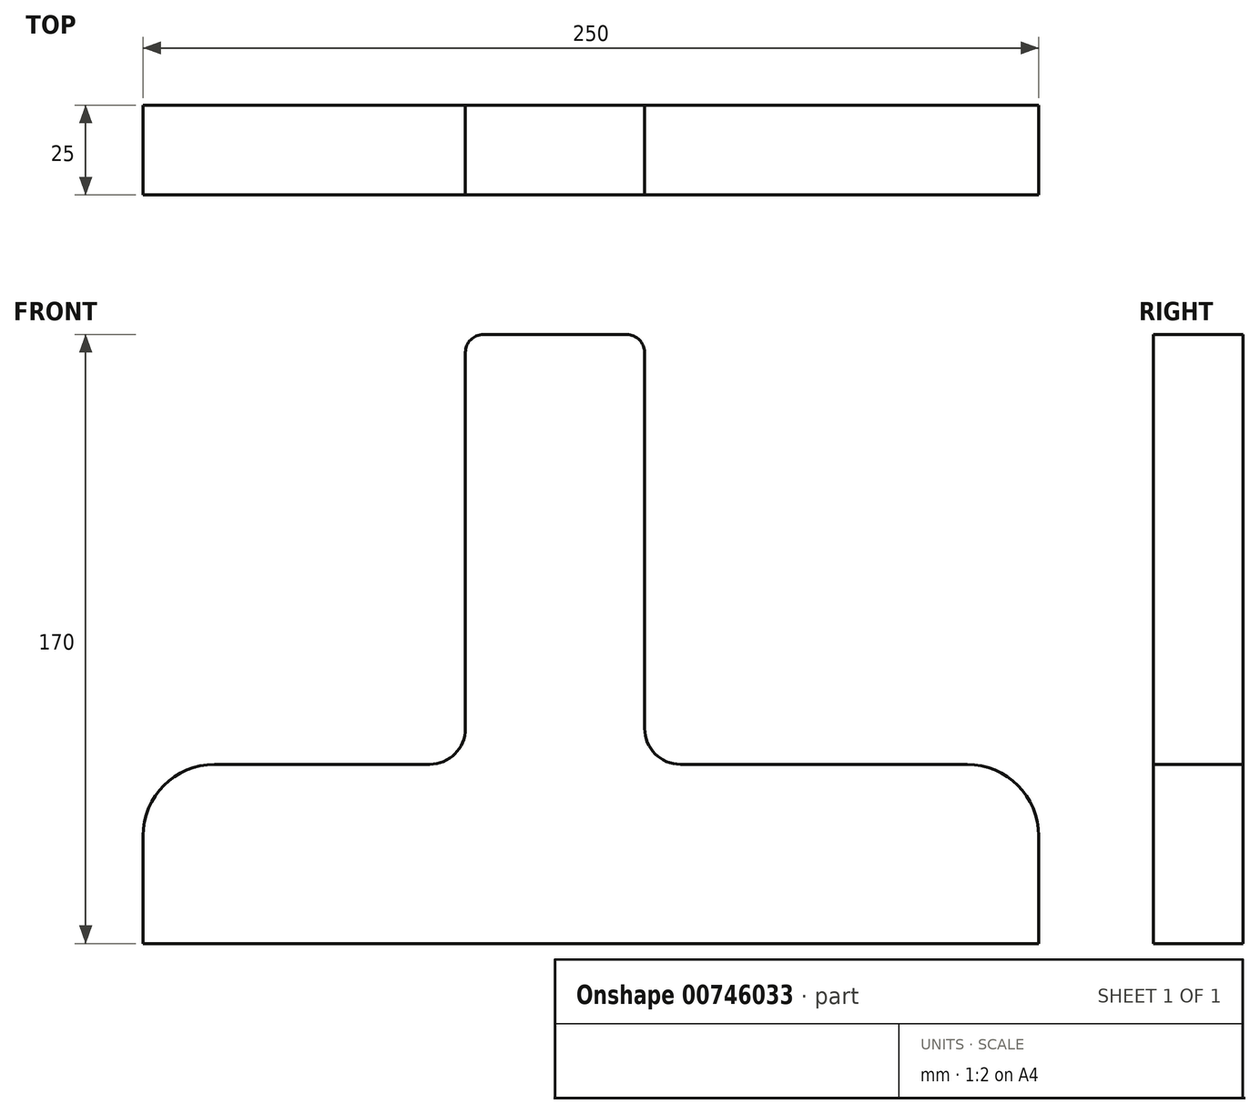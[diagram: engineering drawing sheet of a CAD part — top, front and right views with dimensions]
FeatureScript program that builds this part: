
annotation { "Feature Type Name" : "Feature", "Feature Type Description" : "" }
export const myFeature = defineFeature(function(context is Context, id is Id, definition is map)
    precondition{}
    {
        {
            var Q0;
            Q0=qCreatedBy(makeId("Front.planeOp"),FACE);
            var sketch = newSketch(context, id + "F0", { "sketchPlane" : qUnion([Q0])});
            skLineSegment(sketch, "E0", {"start": v(104, -275.58) * mm, "end": v(354, -275.58) * mm});
            skLineSegment(sketch, "E1", {"start": v(354, -275.58) * mm, "end": v(354, -245.58) * mm});
            skLineSegment(sketch, "E2", {"start": v(334, -225.58) * mm, "end": v(254, -225.58) * mm});
            skLineSegment(sketch, "E3", {"start": v(244, -215.58) * mm, "end": v(244, -110.58) * mm});
            skLineSegment(sketch, "E4", {"start": v(239, -105.58) * mm, "end": v(199, -105.58) * mm});
            skLineSegment(sketch, "E5", {"start": v(194, -110.58) * mm, "end": v(194, -215.58) * mm});
            skLineSegment(sketch, "E6", {"start": v(184, -225.58) * mm, "end": v(124, -225.58) * mm});
            skLineSegment(sketch, "E7", {"start": v(104, -245.58) * mm, "end": v(104, -275.58) * mm});
            skPoint(sketch, "E8.visualSharp", {"position": v(244, -225.58) * mm});
            skArc(sketch, "E8.filletArc", {"start": v(244, -215.58) * mm, "mid": v(246.92, -222.65) * mm, "end": v(254, -225.58) * mm});
            skPoint(sketch, "E9.visualSharp", {"position": v(194, -225.58) * mm});
            skArc(sketch, "E9.filletArc", {"start": v(184, -225.58) * mm, "mid": v(191.06, -222.65) * mm, "end": v(194, -215.58) * mm});
            skPoint(sketch, "E10.visualSharp", {"position": v(354, -225.58) * mm});
            skLineSegment(sketch, "E10.filletArc", {"start": v(354, -225.58) * mm, "end": v(354, -225.58) * mm});
            skPoint(sketch, "E11.visualSharp", {"position": v(104, -225.58) * mm});
            skLineSegment(sketch, "E11.filletArc", {"start": v(104, -225.58) * mm, "end": v(104, -225.58) * mm});
            skArc(sketch, "E12.filletArc", {"start": v(354, -245.58) * mm, "mid": v(348.13, -231.44) * mm, "end": v(334, -225.58) * mm});
            skArc(sketch, "E13.filletArc", {"start": v(124, -225.58) * mm, "mid": v(109.85, -231.44) * mm, "end": v(104, -245.58) * mm});
            skPoint(sketch, "E14.visualSharp", {"position": v(244, -105.58) * mm});
            skArc(sketch, "E14.filletArc", {"start": v(244, -110.58) * mm, "mid": v(242.53, -107.05) * mm, "end": v(239, -105.58) * mm});
            skPoint(sketch, "E15.visualSharp", {"position": v(194, -105.58) * mm});
            skArc(sketch, "E15.filletArc", {"start": v(199, -105.58) * mm, "mid": v(195.46, -107.05) * mm, "end": v(194, -110.58) * mm});
            skSolve(sketch);
        }
        {
            var Q0;
            Q0=makeQuery(id+"F0.imprint","IMPRINT",FACE,{"disambiguationData":[TD([[makeQuery(id+"F0.imprint","IMPRINT",EDGE,{"derivedFrom":sQuery(id+"F0.wireOp",EDGE,"E0")}),1.0]])]});
            extrude(context, id + "F1", {"entities" : qUnion([Q0]), "depth" : 25 * mm, "offsetDistance" : 25 * mm});
        }
    });
